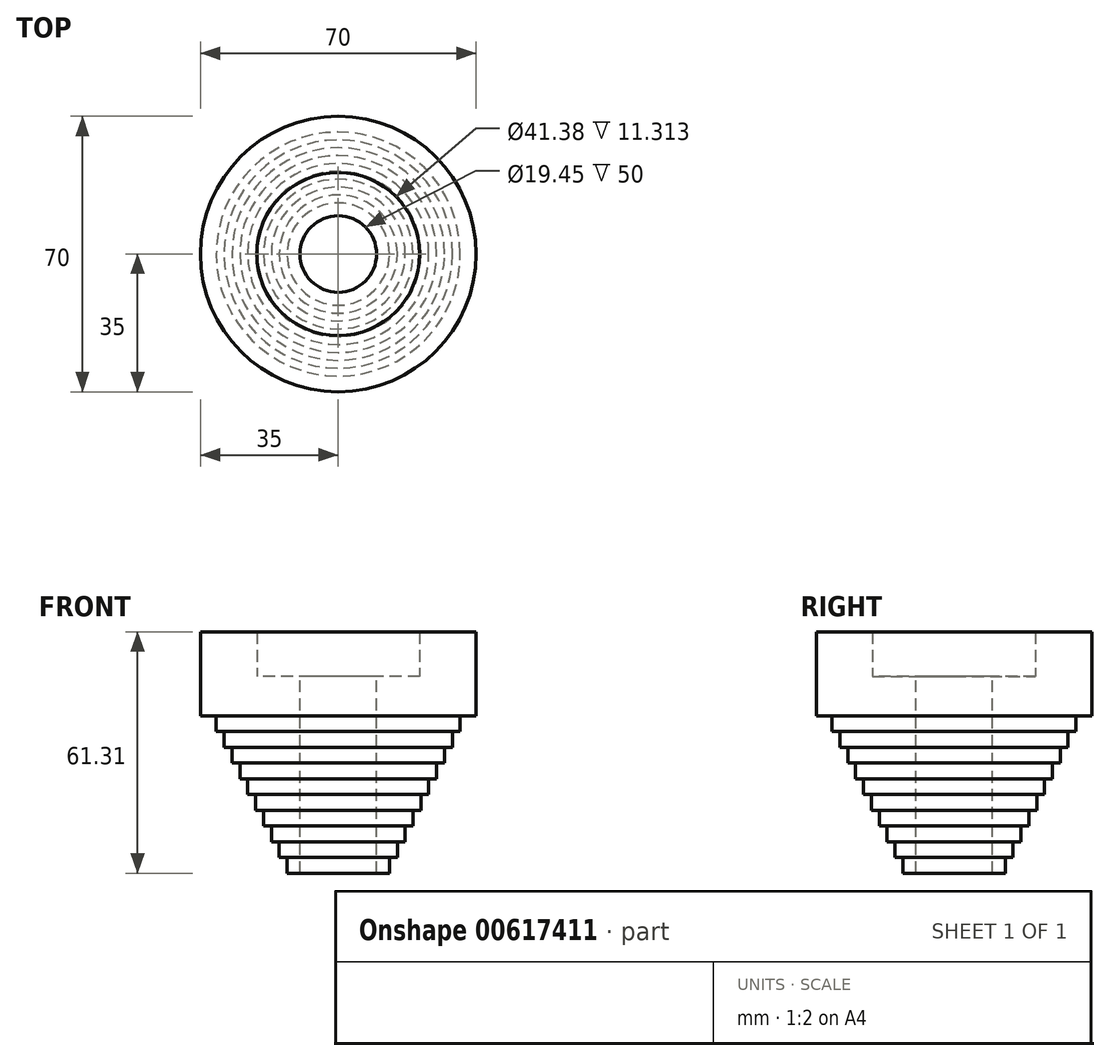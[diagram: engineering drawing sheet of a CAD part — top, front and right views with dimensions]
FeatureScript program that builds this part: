
annotation { "Feature Type Name" : "Feature", "Feature Type Description" : "" }
export const myFeature = defineFeature(function(context is Context, id is Id, definition is map)
    precondition{}
    {
        {
            var Q0;
            Q0=qCreatedBy(makeId("Top.planeOp"),FACE);
            var sketch = newSketch(context, id + "F0", { "sketchPlane" : qUnion([Q0])});
            skCircle(sketch, "E0", {"center": v(0, 0) * mm, "radius": 9.53 * mm});
            skCircle(sketch, "E1.0", {"center": v(0, 0) * mm, "radius": 9.73 * mm});
            skCircle(sketch, "E2.0", {"center": v(0, 0) * mm, "radius": 35 * mm});
            skCircle(sketch, "E3", {"center": v(0, 0) * mm, "radius": 20.69 * mm});
            skSolve(sketch);
        }
        {
            var Q0;
            Q0 = qSketchRegion(id + "F0", true);
            extrude(context, id + "F1", {"entities" : qUnion([Q0]), "depth" : 11.3 * mm, "offsetDistance" : 25 * mm});
        }
        {
            var Q0;
            Q0=makeQuery(id+"F0.imprint","IMPRINT",FACE,{"disambiguationData":[TD([[makeQuery(id+"F0.imprint","IMPRINT",EDGE,{"derivedFrom":sQuery(id+"F0.wireOp",EDGE,"E1.0")}),-1.0]])]});
            var Q1;
            Q1=makeQuery(id+"F0.imprint","IMPRINT",FACE,{"disambiguationData":[TD([[makeQuery(id+"F0.imprint","IMPRINT",EDGE,{"derivedFrom":sQuery(id+"F0.wireOp",EDGE,"E2.0")}),1.0]])]});
            extrude(context, id + "F2", {"entities" : qUnion([Q0, Q1]), "operationType" : NewBodyOperationType.ADD, "oppositeDirection" : true, "depth" : 50 * mm, "offsetDistance" : 25 * mm});
        }
        {
            var Q0;
            Q0=makeQuery(id+"F2.opExtrude","CAP_FACE",FACE,{"disambiguationData":[OSD([sQuery(id+"F0.wireOp",EDGE,"E1.0"),sQuery(id+"F0.wireOp",EDGE,"E2.0")])],"isStart":false});
            var sketch = newSketch(context, id + "F3", { "sketchPlane" : qUnion([Q0])});
            skCircle(sketch, "E4", {"center": v(0, 0) * mm, "radius": 13 * mm});
            skCircle(sketch, "E5.0", {"center": v(0, 0) * mm, "radius": 15 * mm});
            skCircle(sketch, "E6.0", {"center": v(0, 0) * mm, "radius": 17 * mm});
            skCircle(sketch, "E7.0", {"center": v(0, 0) * mm, "radius": 19 * mm});
            skCircle(sketch, "E8.0", {"center": v(0, 0) * mm, "radius": 21 * mm});
            skCircle(sketch, "E9.0", {"center": v(0, 0) * mm, "radius": 23 * mm});
            skCircle(sketch, "E10.0", {"center": v(0, 0) * mm, "radius": 25 * mm});
            skCircle(sketch, "E11.0", {"center": v(0, 0) * mm, "radius": 27 * mm});
            skCircle(sketch, "E12.0", {"center": v(0, 0) * mm, "radius": 29 * mm});
            skCircle(sketch, "E13.0", {"center": v(0, 0) * mm, "radius": 31 * mm});
            skSolve(sketch);
        }
        {
            var Q0;
            Q0=makeQuery(id+"F3.imprint","IMPRINT",FACE,{"disambiguationData":[TD([[makeQuery(id+"F3.imprint","IMPRINT",EDGE,{"derivedFrom":sQuery(id+"F3.wireOp",EDGE,"E4")}),-1.0]])]});
            extrude(context, id + "F4", {"entities" : qUnion([Q0]), "operationType" : NewBodyOperationType.REMOVE, "oppositeDirection" : true, "depth" : 4 * mm, "offsetDistance" : 25 * mm});
        }
        {
            var Q0;
            Q0=makeQuery(id+"F3.imprint","IMPRINT",FACE,{"disambiguationData":[TD([[makeQuery(id+"F3.imprint","IMPRINT",EDGE,{"derivedFrom":sQuery(id+"F3.wireOp",EDGE,"E5.0")}),-1.0]])]});
            extrude(context, id + "F5", {"entities" : qUnion([Q0]), "operationType" : NewBodyOperationType.REMOVE, "oppositeDirection" : true, "depth" : 8 * mm, "offsetDistance" : 25 * mm});
        }
        {
            var Q0;
            Q0=makeQuery(id+"F3.imprint","IMPRINT",FACE,{"disambiguationData":[TD([[makeQuery(id+"F3.imprint","IMPRINT",EDGE,{"derivedFrom":sQuery(id+"F3.wireOp",EDGE,"E6.0")}),-1.0]])]});
            extrude(context, id + "F6", {"entities" : qUnion([Q0]), "operationType" : NewBodyOperationType.REMOVE, "oppositeDirection" : true, "depth" : 12 * mm, "offsetDistance" : 25 * mm});
        }
        {
            var Q0;
            Q0=makeQuery(id+"F3.imprint","IMPRINT",FACE,{"disambiguationData":[TD([[makeQuery(id+"F3.imprint","IMPRINT",EDGE,{"derivedFrom":sQuery(id+"F3.wireOp",EDGE,"E7.0")}),-1.0]])]});
            extrude(context, id + "F7", {"entities" : qUnion([Q0]), "operationType" : NewBodyOperationType.REMOVE, "oppositeDirection" : true, "depth" : 16 * mm, "offsetDistance" : 25 * mm});
        }
        {
            var Q0;
            Q0=makeQuery(id+"F3.imprint","IMPRINT",FACE,{"disambiguationData":[TD([[makeQuery(id+"F3.imprint","IMPRINT",EDGE,{"derivedFrom":sQuery(id+"F3.wireOp",EDGE,"E8.0")}),-1.0]])]});
            extrude(context, id + "F8", {"entities" : qUnion([Q0]), "operationType" : NewBodyOperationType.REMOVE, "oppositeDirection" : true, "depth" : 20 * mm, "offsetDistance" : 25 * mm});
        }
        {
            var Q0;
            Q0=makeQuery(id+"F3.imprint","IMPRINT",FACE,{"disambiguationData":[TD([[makeQuery(id+"F3.imprint","IMPRINT",EDGE,{"derivedFrom":sQuery(id+"F3.wireOp",EDGE,"E9.0")}),-1.0]])]});
            extrude(context, id + "F9", {"entities" : qUnion([Q0]), "operationType" : NewBodyOperationType.REMOVE, "oppositeDirection" : true, "depth" : 24 * mm, "offsetDistance" : 25 * mm});
        }
        {
            var Q0;
            Q0=makeQuery(id+"F3.imprint","IMPRINT",FACE,{"disambiguationData":[TD([[makeQuery(id+"F3.imprint","IMPRINT",EDGE,{"derivedFrom":sQuery(id+"F3.wireOp",EDGE,"E10.0")}),-1.0]])]});
            extrude(context, id + "F10", {"entities" : qUnion([Q0]), "operationType" : NewBodyOperationType.REMOVE, "oppositeDirection" : true, "depth" : 28 * mm, "offsetDistance" : 25 * mm});
        }
        {
            var Q0;
            Q0=makeQuery(id+"F3.imprint","IMPRINT",FACE,{"disambiguationData":[TD([[makeQuery(id+"F3.imprint","IMPRINT",EDGE,{"derivedFrom":sQuery(id+"F3.wireOp",EDGE,"E11.0")}),-1.0]])]});
            extrude(context, id + "F11", {"entities" : qUnion([Q0]), "operationType" : NewBodyOperationType.REMOVE, "oppositeDirection" : true, "depth" : 32 * mm, "offsetDistance" : 25 * mm});
        }
        {
            var Q0;
            Q0=makeQuery(id+"F3.imprint","IMPRINT",FACE,{"disambiguationData":[TD([[makeQuery(id+"F3.imprint","IMPRINT",EDGE,{"derivedFrom":sQuery(id+"F3.wireOp",EDGE,"E12.0")}),-1.0]])]});
            extrude(context, id + "F12", {"entities" : qUnion([Q0]), "operationType" : NewBodyOperationType.REMOVE, "oppositeDirection" : true, "depth" : 36 * mm, "offsetDistance" : 25 * mm});
        }
        {
            var Q0;
            Q0=makeQuery(id+"F12.opExtrude","CAP_FACE",FACE,{"disambiguationData":[OSD([sQuery(id+"F3.wireOp",EDGE,"E12.0"),sQuery(id+"F3.wireOp",EDGE,"E13.0")])],"isStart":false});
            var Q1;
            Q1=makeQuery(id+"F3.imprint","IMPRINT",FACE,{"disambiguationData":[TD([[makeQuery(id+"F3.imprint","IMPRINT",EDGE,{"derivedFrom":sQuery(id+"F3.wireOp",EDGE,"E13.0")}),-1.0]])]});
            extrude(context, id + "F13", {"entities" : qUnion([Q0, Q1]), "operationType" : NewBodyOperationType.REMOVE, "oppositeDirection" : true, "depth" : 40 * mm, "offsetDistance" : 25 * mm});
        }
    });
